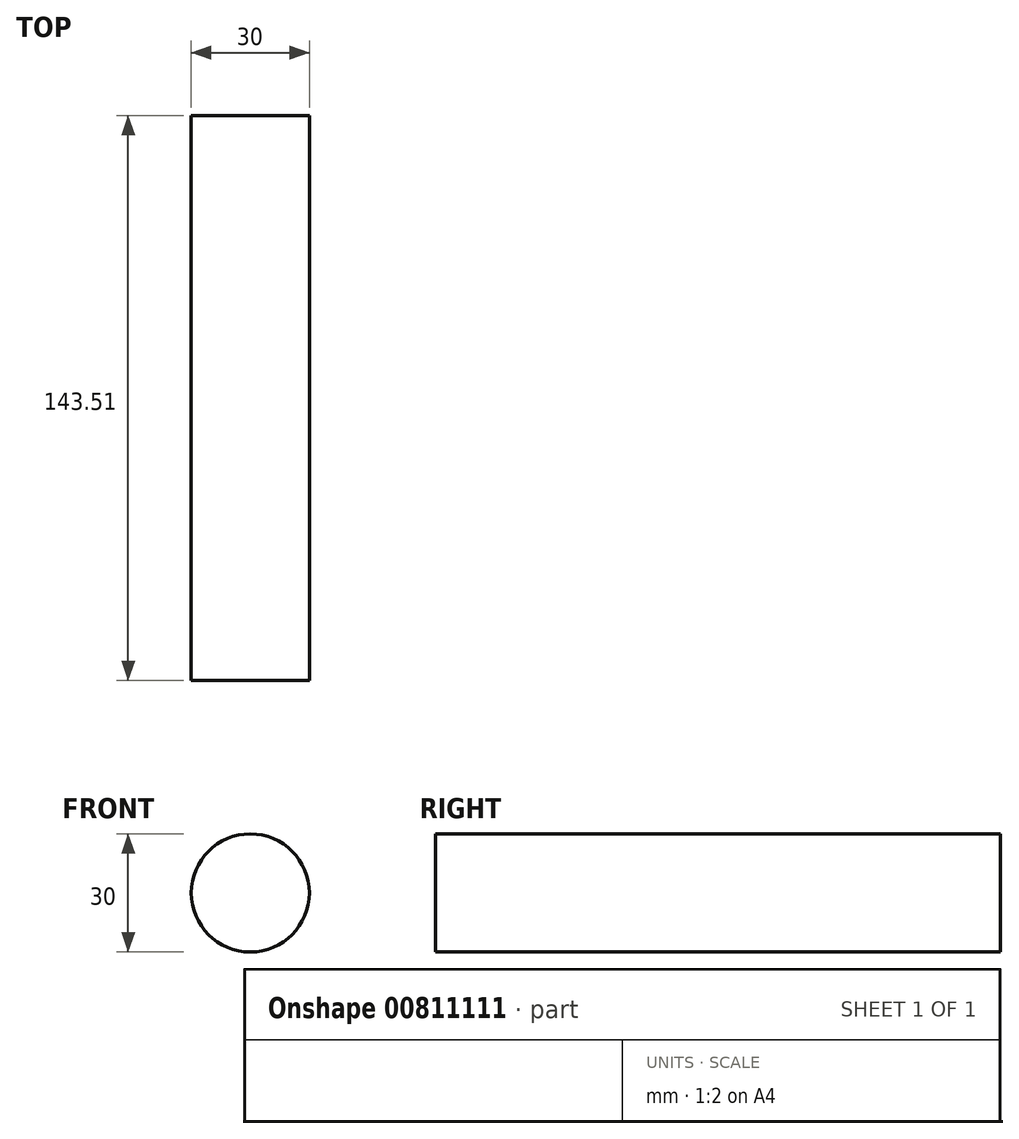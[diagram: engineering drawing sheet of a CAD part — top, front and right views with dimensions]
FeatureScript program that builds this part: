
annotation { "Feature Type Name" : "Feature", "Feature Type Description" : "" }
export const myFeature = defineFeature(function(context is Context, id is Id, definition is map)
    precondition{}
    {
        {
            var Q0;
            Q0=qCreatedBy(makeId("Front.planeOp"),FACE);
            var sketch = newSketch(context, id + "F0", { "sketchPlane" : qUnion([Q0])});
            skCircle(sketch, "E0", {"center": v(0, 0) * mm, "radius": 15 * mm});
            skSolve(sketch);
        }
        {
            var Q0;
            Q0 = qSketchRegion(id + "F0", true);
            extrude(context, id + "F1", {"entities" : qUnion([Q0]), "depth" : 143.5 * mm, "offsetDistance" : 25.4 * mm});
        }
    });
